# Revit family: Faucet-Lavatory-Spout-KOHLER-ARTIFACTS-K-72758T
name_source: partatom
category: Plumbing Fixtures
revit_build: Autodesk Revit 2017 (Build: 20160225_1515(x64)
units: mm (PartAtom-declared; Revit-internal decimal feet)

## family parameters
Cut with Voids When Loaded = No
Host = Face
OmniClass Number = 23.31.11.00
OmniClass Title = Faucets
Part Type = Normal
Room Calculation Point = No
Round Connector Dimension = Use Diameter
Shared = No

## types (10) — shared parameters
ADA Compliant = No
Assembly Code = D2010
CW Connection = No
Cold Water Inlet = Cold Water Inlet
Date Modified = 08/19/2020
Default Elevation = 36"
Description = 8 inch basin tap out of the mouth curved outlet
Drain Included = Yes
HW Connection = No
Height = 4 11/16"
Hot Water Inlet = Hot Water Inlet
Length = 5 3/8"
Manufacturer = KOHLER Co.
Master Format 2014 = 22 41 39
Master Format 2014 Name = Residential Faucets, Supplies, and Trim
Material = Premium Metal Construction
Product Documentation Link = https://files.kohler.com.cn
Product Name = ARTIFACTS
Product Page URL = https://www.kohler.com.cn
Spout Reach = 5 3/8"
URL = http://www.kohler.com.cn
Vent Connection = No
Waste Connection = No
Waste Water Outlet = Waste Water Outlet
WaterSense Certified = No
Width = 3 1/8"

## per-type parameters (varying)
| type | Finish | Flow Rate | Model | Pressure | Type |
| CP-Polished Chrome | Kohler-Metal-CP-Polished_Chrome | 0 GPM | K-72758T-CP | 0.00 psi | 1 |
| BV-Roman Copper | Kohler-Metal-BV-Brushed_Bronze | 1 GPM | K-72758T-BV | 60.00 psi | 2 |
| RGD-Rose Gold | Kohler-Metal-RGD-Polished_Rose_Gold | 1 GPM | K-72758T-RGD | 60.00 psi | 3 |
| 2BZ-Elegant Black | Kohler-Metal-2BZ-Oil_Rubbed_Bronze | 1 GPM | K-72758T-2BZ | 60.00 psi | 4 |
| AF-Flange Gold | Kohler-Metal-AF-Vibrant_French_Gold | 1 GPM | K-72758T-AF | 60.00 psi | 5 |
| BN-Roman Silver | Kohler-Metal-BN-Vibrant_Brushed_Nickel | 1 GPM | K-72758T-BN | 60.00 psi | 6 |
| SN-Champagne Gold | Kohler-Metal-SN-Vibrant_Polished_Nickel | 1 GPM | K-72758-SN | 60.00 psi | 7 |
| PGD-Eternal Gold | Kohler-Metal-PGD-Modern_Polished_Gold | 1 GPM | K-72758-PGD | 60.00 psi | 8 |
| TT-Titanium Air Silve | Kohler-Metal-TT-Vibrant_Titanium | 1 GPM | K-72758-TT | 60.00 psi | 9 |
| 2BL-Primary Black | Kohler-Metal-2BL-Original_Black | 1 GPM | K-72758-2BL | 60.00 psi | 10 |

## geometry (parser evidence)
native form markers: Sweep x5
no freeform markers — native parametric forms only
